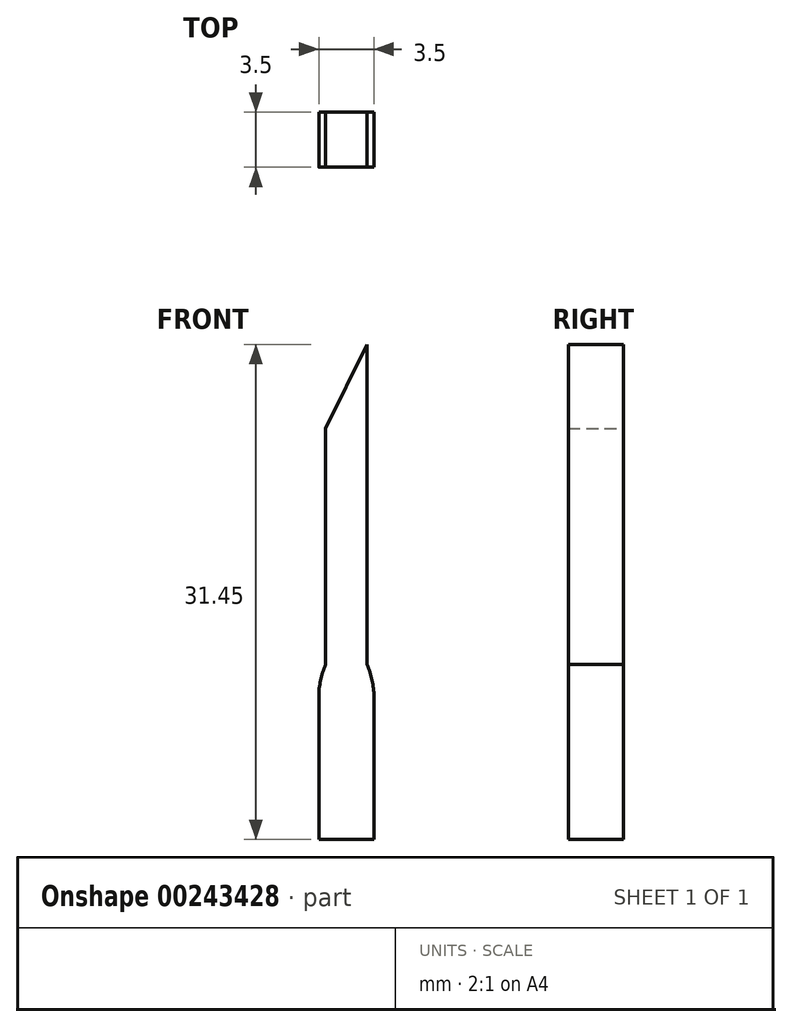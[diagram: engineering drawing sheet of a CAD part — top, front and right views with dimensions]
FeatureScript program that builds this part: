
annotation { "Feature Type Name" : "Feature", "Feature Type Description" : "" }
export const myFeature = defineFeature(function(context is Context, id is Id, definition is map)
    precondition{}
    {
        {
            var Q0;
            Q0=qCreatedBy(makeId("Front.planeOp"),FACE);
            var sketch = newSketch(context, id + "F0", { "sketchPlane" : qUnion([Q0])});
            skLineSegment(sketch, "E0", {"start": v(-16.48, -35.8) * mm, "end": v(-16.48, -24.7) * mm});
            skLineSegment(sketch, "E1", {"start": v(-16.48, -35.8) * mm, "end": v(-12.98, -35.8) * mm});
            skLineSegment(sketch, "E2", {"start": v(-12.98, -35.8) * mm, "end": v(-16.48, -35.8) * mm});
            skArc(sketch, "E3", {"start": v(-16.48, -35.8) * mm, "mid": v(-14.73, -36.73) * mm, "end": v(-12.98, -35.8) * mm});
            skLineSegment(sketch, "E4", {"start": v(-12.98, -35.8) * mm, "end": v(-12.98, -24.7) * mm});
            skLineSegment(sketch, "E5", {"start": v(-16.48, -24.7) * mm, "end": v(-12.98, -24.7) * mm});
            skLineSegment(sketch, "E6", {"start": v(-16.48, -24.7) * mm, "end": v(-16.04, -24.7) * mm});
            skLineSegment(sketch, "E7", {"start": v(-16.04, -24.7) * mm, "end": v(-16.04, -9.7) * mm});
            skLineSegment(sketch, "E8", {"start": v(-12.98, -24.7) * mm, "end": v(-13.41, -24.7) * mm});
            skLineSegment(sketch, "E9", {"start": v(-13.41, -24.7) * mm, "end": v(-13.41, -4.35) * mm});
            skLineSegment(sketch, "E10", {"start": v(-13.41, -4.35) * mm, "end": v(-16.04, -9.7) * mm});
            skSolve(sketch);
        }
        {
            var Q0;
            Q0=makeQuery(id+"F0.imprint","IMPRINT",FACE,{"disambiguationData":[TD([[makeQuery(id+"F0.imprint","IMPRINT",EDGE,{"derivedFrom":sQuery(id+"F0.wireOp",EDGE,"E2")}),1.0]])]});
            var Q1;
            Q1=makeQuery(id+"F0.imprint","IMPRINT",FACE,{"disambiguationData":[TD([[makeQuery(id+"F0.imprint","IMPRINT",EDGE,{"derivedFrom":sQuery(id+"F0.wireOp",EDGE,"E5")}),1.0]])]});
            var Q2;
            Q2=makeQuery(id+"F0.imprint","IMPRINT",FACE,{"disambiguationData":[TD([[makeQuery(id+"F0.imprint","IMPRINT",EDGE,{"derivedFrom":sQuery(id+"F0.wireOp",EDGE,"E0")}),-1.0]])]});
            extrude(context, id + "F1", {"entities" : qUnion([Q0, Q1, Q2]), "depth" : 3.5 * mm});
        }
        {
            var Q0;
            Q0=makeQuery(id+"F1.opExtrude","SWEPT_EDGE",EDGE,{"disambiguationData":[OSD([sQuery(id+"F0.wireOp",EDGE,"E0"),sQuery(id+"F0.wireOp",EDGE,"E6")])]});
            var Q1;
            Q1=makeQuery(id+"F1.opExtrude","SWEPT_EDGE",EDGE,{"disambiguationData":[OSD([sQuery(id+"F0.wireOp",EDGE,"E4"),sQuery(id+"F0.wireOp",EDGE,"E8")])]});
            fillet(context, id + "F2", {"entities" : qUnion([Q0, Q1]), "radius" : 5 * mm, "tangentPropagation" : true, "allowEdgeOverflow" : false});
        }
    });
